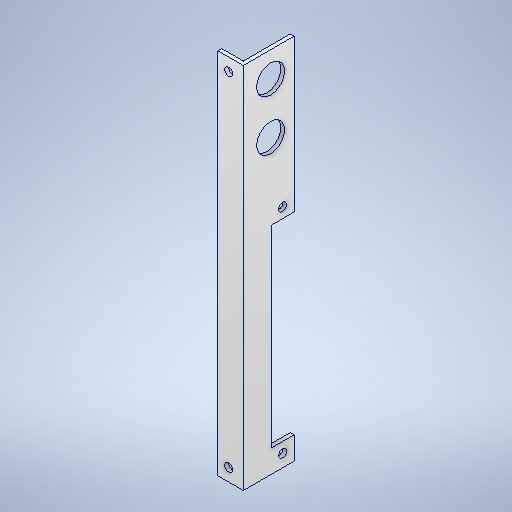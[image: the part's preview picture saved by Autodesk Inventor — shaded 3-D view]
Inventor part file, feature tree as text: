
AUTODESK INVENTOR PART (.ipt)
format: ipt  version: 2025 (Build 290162000, 162)  size: 313,856 bytes
history: native  units: mm
features: sketch x5, hole x3, projected_geometry x3, extrude x2, other x1
ambient origin geometry x8: Origin, YZ Plane, XZ Plane, XY Plane, X Axis, Y Axis, Z Axis, Center Point
bodies: Body1 (feature_tree)
feature tree (14):
  other  "Těleso1"
  extrude  "Vysunutí1"  Depth=20.0mm
  hole  "Díra1"  [1 undecoded]
  hole  "Díra7"  [1 undecoded]
  extrude  "Vysunutí3"  Depth=1.5mm
  hole  "Díra8"  [1 undecoded]
  sketch  "Náčrt1"
  sketch  "Náčrt2"
  projected_geometry  "Promítnutá smyčka1"
  sketch  "Náčrt9"
  sketch  "Náčrt10"
  projected_geometry  "Promítnutá smyčka7"
  sketch  "Náčrt11"
  projected_geometry  "Promítnutá smyčka8"
note: 3 required parameter values undecoded (feature->parameter linkage not recoverable at this tier; creation-order binding heuristic only, values carry confidence <= 0.55)
